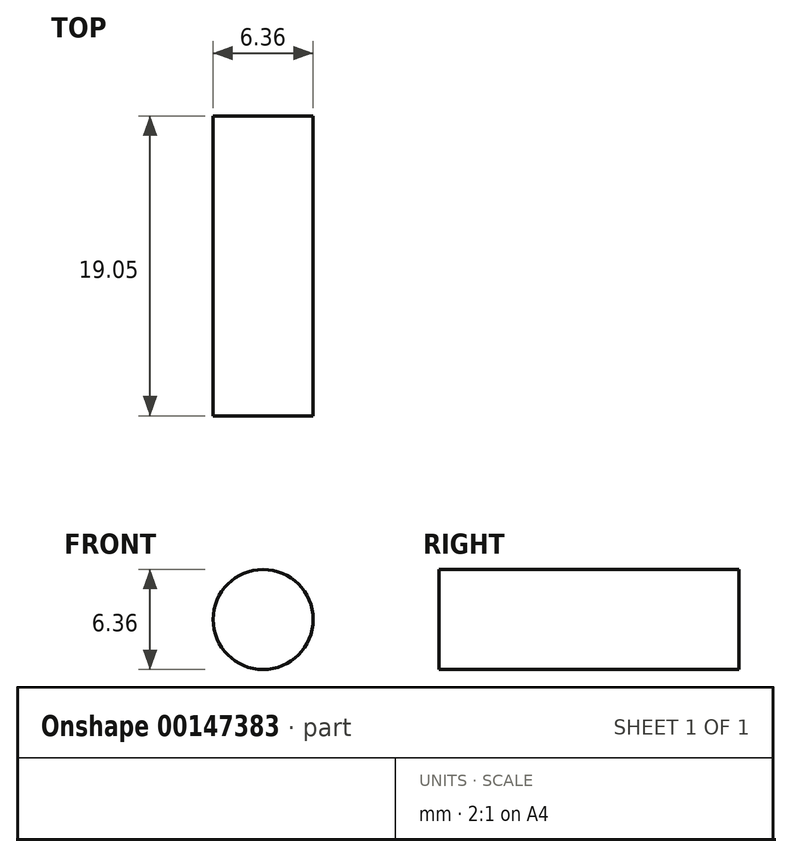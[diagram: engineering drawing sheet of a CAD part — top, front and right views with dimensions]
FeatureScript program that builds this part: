
annotation { "Feature Type Name" : "Feature", "Feature Type Description" : "" }
export const myFeature = defineFeature(function(context is Context, id is Id, definition is map)
    precondition{}
    {
        {
            var Q0;
            Q0=qCreatedBy(makeId("Front.planeOp"),FACE);
            var sketch = newSketch(context, id + "F0", { "sketchPlane" : qUnion([Q0])});
            skCircle(sketch, "E0", {"center": v(0, 0) * mm, "radius": 3.18 * mm});
            skSolve(sketch);
        }
        {
            var Q0;
            Q0 = qSketchRegion(id + "F0", true);
            extrude(context, id + "F1", {"entities" : qUnion([Q0]), "depth" : 19.05 * mm});
        }
    });
